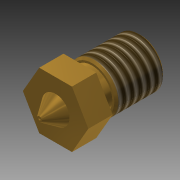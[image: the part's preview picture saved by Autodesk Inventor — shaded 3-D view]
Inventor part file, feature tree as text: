
AUTODESK INVENTOR PART (.ipt)
format: ipt  version: 2015 (Build 190159000, 159)  size: 147,456 bytes
history: native  units: mm
features: sketch x4, hole x3, chamfer x2, other x1, revolve x1, thread x1, extrude x1
ambient origin geometry x8: Origin, YZ Plane, XZ Plane, XY Plane, X Axis, Y Axis, Z Axis, Center Point
bodies: Body1 (feature_tree)
feature tree (13):
  other  "Твердое тело1"
  revolve  "Вращение1"
  chamfer  "Фаска1"  Distance=15.0mm
  thread  "Резьба1"
  sketch  "Эскиз2"
  sketch  "Эскиз3"
  hole  "Отверстие1"  [1 undecoded]
  hole  "Отверстие2"  [1 undecoded]
  chamfer  "Фаска2"  Distance=7.5mm
  hole  "Отверстие3"  [1 undecoded]
  extrude  "Выдавливание1"  Depth=5.0mm
  sketch  "Эскиз1"
  sketch  "Эскиз4"
note: 3 required parameter values undecoded (feature->parameter linkage not recoverable at this tier; creation-order binding heuristic only, values carry confidence <= 0.55)
